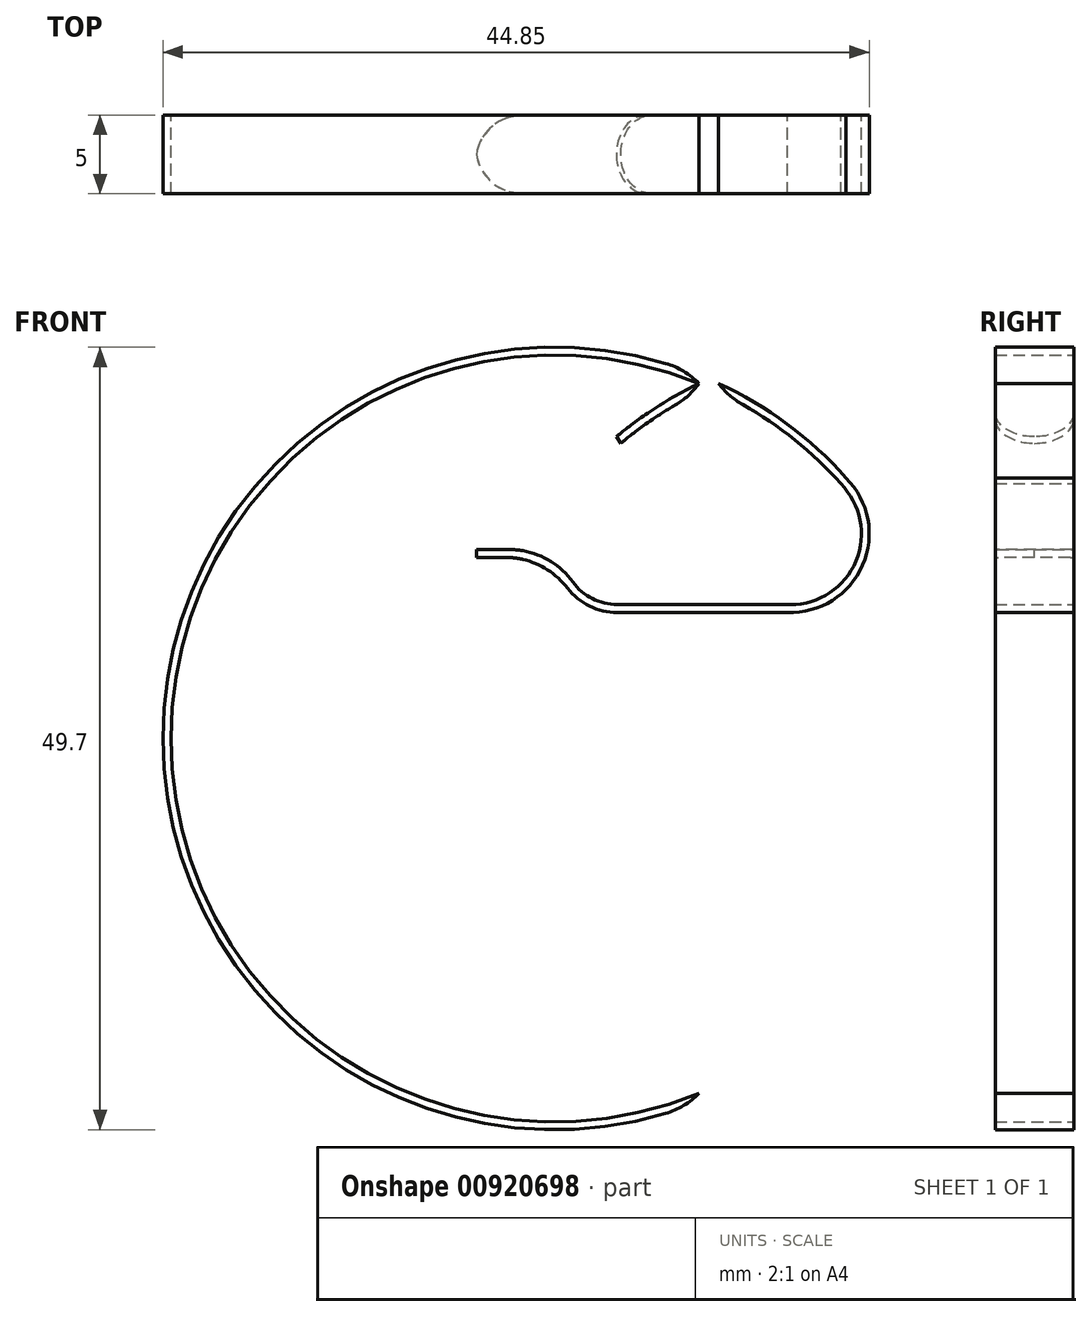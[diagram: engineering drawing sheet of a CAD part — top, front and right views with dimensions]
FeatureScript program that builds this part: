
annotation { "Feature Type Name" : "Feature", "Feature Type Description" : "" }
export const myFeature = defineFeature(function(context is Context, id is Id, definition is map)
    precondition{}
    {
        {
            var Q0;
            Q0=qCreatedBy(makeId("Front.planeOp"),FACE);
            var sketch = newSketch(context, id + "F0", { "sketchPlane" : qUnion([Q0])});
            skLineSegment(sketch, "E0.bottom", {"start": v(10, 7) * mm, "end": v(-10, 7) * mm});
            skLineSegment(sketch, "E0.top", {"start": v(10, -7) * mm, "end": v(-10, -7) * mm});
            skLineSegment(sketch, "E0.left", {"start": v(10, 7) * mm, "end": v(10, -7) * mm});
            skLineSegment(sketch, "E0.right", {"start": v(-10, 7) * mm, "end": v(-10, -7) * mm});
            skPoint(sketch, "E0.middle", {"position": v(0, 0) * mm});
            skLineSegment(sketch, "E1", {"start": v(10, -7) * mm, "end": v(5, -7) * mm});
            skLineSegment(sketch, "E2", {"start": v(5, -7) * mm, "end": v(5, -2) * mm});
            skCircle(sketch, "E3", {"center": v(5, -2) * mm, "radius": 5 * mm});
            skLineSegment(sketch, "E4", {"start": v(-10, -7) * mm, "end": v(-6, -7) * mm});
            skLineSegment(sketch, "E5", {"start": v(-6, -7) * mm, "end": v(-6, -3) * mm});
            skCircle(sketch, "E6", {"center": v(-6, -3) * mm, "radius": 4 * mm});
            skLineSegment(sketch, "E7", {"start": v(-10, -7) * mm, "end": v(-10, -15) * mm});
            skLineSegment(sketch, "E8", {"start": v(10, -7) * mm, "end": v(10, -15) * mm});
            skCircle(sketch, "E9", {"center": v(-10, -15) * mm, "radius": 24.85 * mm});
            skCircle(sketch, "E10", {"center": v(10, -15) * mm, "radius": 25 * mm});
            skCircle(sketch, "E11", {"center": v(-10, -15) * mm, "radius": 24.35 * mm});
            skCircle(sketch, "E12", {"center": v(10, -15) * mm, "radius": 24.5 * mm});
            skLineSegment(sketch, "E13", {"start": v(-6.06, 4.16) * mm, "end": v(-5.78, 3.74) * mm});
            skCircle(sketch, "E14", {"center": v(-6, -3) * mm, "radius": 3.5 * mm});
            skCircle(sketch, "E15", {"center": v(5, -2) * mm, "radius": 4.5 * mm});
            skLineSegment(sketch, "E16", {"start": v(-6, -3) * mm, "end": v(-15, -3) * mm});
            skLineSegment(sketch, "E17", {"start": v(-15, -3) * mm, "end": v(-15, -3.5) * mm});
            skLineSegment(sketch, "E18", {"start": v(-15, -3.5) * mm, "end": v(-6, -3.5) * mm});
            skLineSegment(sketch, "E19", {"start": v(-6, -6.5) * mm, "end": v(5, -6.5) * mm});
            skLineSegment(sketch, "E20", {"start": v(4.8, -6.37) * mm, "end": v(4.8, -7.22) * mm});
            skLineSegment(sketch, "E21", {"start": v(7.96, 0.92) * mm, "end": v(8.96, 2.01) * mm});
            skSolve(sketch);
        }
        {
            var Q0;
            {var subQ0=sQuery(id+"F0.wireOp",EDGE,"E3");var subQ3=makeQuery(id+"F0.imprint","INTERSECT",VERTEX,{"derivedFrom":[sQuery(id+"F0.wireOp",EDGE,"E0.left"),subQ0]});Q0=makeQuery(id+"F0.imprint","IMPRINT",FACE,{"disambiguationData":[TD([[makeQuery(id+"F0.imprint","IMPRINT",EDGE,{"disambiguationData":[TD([[subQ3,-1.0]])],"derivedFrom":subQ0}),1.0]])]});}
            var Q1;
            {var subQ0=sQuery(id+"F0.wireOp",EDGE,"E3");var subQ5=sQuery(id+"F0.wireOp",EDGE,"E20");var subQ6=makeQuery(id+"F0.imprint","INTERSECT",VERTEX,{"derivedFrom":[subQ0,subQ5]});Q1=makeQuery(id+"F0.imprint","IMPRINT",FACE,{"disambiguationData":[TD([[makeQuery(id+"F0.imprint","IMPRINT",EDGE,{"disambiguationData":[TD([[subQ6,1.0]])],"derivedFrom":subQ5}),1.0]])]});}
            var Q2;
            {var subQ0=sQuery(id+"F0.wireOp",EDGE,"E19");var subQ1=sQuery(id+"F0.wireOp",EDGE,"E3");var subQ2=makeQuery(id+"F0.imprint","INTERSECT",VERTEX,{"derivedFrom":[subQ1,subQ0]});Q2=makeQuery(id+"F0.imprint","IMPRINT",FACE,{"disambiguationData":[TD([[makeQuery(id+"F0.imprint","IMPRINT",EDGE,{"disambiguationData":[TD([[subQ2,-1.0]])],"derivedFrom":subQ1}),1.0]])]});}
            var Q3;
            {var subQ0=sQuery(id+"F0.wireOp",EDGE,"E19");var subQ1=sQuery(id+"F0.wireOp",EDGE,"E3");var subQ2=makeQuery(id+"F0.imprint","INTERSECT",VERTEX,{"derivedFrom":[subQ1,subQ0]});Q3=makeQuery(id+"F0.imprint","IMPRINT",FACE,{"disambiguationData":[TD([[makeQuery(id+"F0.imprint","IMPRINT",EDGE,{"disambiguationData":[TD([[subQ2,-1.0]])],"derivedFrom":subQ1}),-1.0]])]});}
            var Q4;
            {var subQ0=sQuery(id+"F0.wireOp",EDGE,"E11");var subQ1=sQuery(id+"F0.wireOp",EDGE,"E3");var subQ2=makeQuery(id+"F0.imprint","INTERSECT",VERTEX,{"disambiguationData":[OD(0.0)],"derivedFrom":[subQ1,subQ0]});Q4=makeQuery(id+"F0.imprint","IMPRINT",FACE,{"disambiguationData":[TD([[makeQuery(id+"F0.imprint","IMPRINT",EDGE,{"disambiguationData":[TD([[subQ2,-1.0]])],"derivedFrom":subQ1}),1.0]])]});}
            var Q5;
            {var subQ0=sQuery(id+"F0.wireOp",EDGE,"E21");var subQ1=sQuery(id+"F0.wireOp",EDGE,"E3");var subQ2=makeQuery(id+"F0.imprint","INTERSECT",VERTEX,{"derivedFrom":[subQ1,subQ0]});Q5=makeQuery(id+"F0.imprint","IMPRINT",FACE,{"disambiguationData":[TD([[makeQuery(id+"F0.imprint","IMPRINT",EDGE,{"disambiguationData":[TD([[subQ2,-1.0]])],"derivedFrom":subQ1}),1.0]])]});}
            var Q6;
            {var subQ1=sQuery(id+"F0.wireOp",EDGE,"E0.bottom");var subQ7=sQuery(id+"F0.wireOp",EDGE,"E9");var subQ9=makeQuery(id+"F0.imprint","INTERSECT",VERTEX,{"derivedFrom":[subQ1,subQ7]});Q6=makeQuery(id+"F0.imprint","IMPRINT",FACE,{"disambiguationData":[TD([[makeQuery(id+"F0.imprint","IMPRINT",EDGE,{"disambiguationData":[TD([[subQ9,-1.0]])],"derivedFrom":subQ1}),1.0]])]});}
            var Q7;
            {var subQ0=sQuery(id+"F0.wireOp",EDGE,"E6");var subQ3=sQuery(id+"F0.wireOp",EDGE,"E19");var subQ5=makeQuery(id+"F0.imprint","INTERSECT",VERTEX,{"derivedFrom":[subQ0,subQ3]});Q7=makeQuery(id+"F0.imprint","IMPRINT",FACE,{"disambiguationData":[TD([[makeQuery(id+"F0.imprint","IMPRINT",EDGE,{"disambiguationData":[TD([[subQ5,1.0]])],"derivedFrom":subQ3}),-1.0]])]});}
            var Q8;
            {var subQ0=sQuery(id+"F0.wireOp",EDGE,"E6");var subQ5=sQuery(id+"F0.wireOp",EDGE,"E18");var subQ6=makeQuery(id+"F0.imprint","INTERSECT",VERTEX,{"derivedFrom":[subQ0,subQ5]});Q8=makeQuery(id+"F0.imprint","IMPRINT",FACE,{"disambiguationData":[TD([[makeQuery(id+"F0.imprint","IMPRINT",EDGE,{"disambiguationData":[TD([[subQ6,-1.0]])],"derivedFrom":subQ5}),-1.0]])]});}
            var Q9;
            {var subQ0=sQuery(id+"F0.wireOp",EDGE,"E18");var subQ5=sQuery(id+"F0.wireOp",EDGE,"E14");var subQ6=makeQuery(id+"F0.imprint","INTERSECT",VERTEX,{"derivedFrom":[subQ5,subQ0]});Q9=makeQuery(id+"F0.imprint","IMPRINT",FACE,{"disambiguationData":[TD([[makeQuery(id+"F0.imprint","IMPRINT",EDGE,{"disambiguationData":[TD([[subQ6,1.0]])],"derivedFrom":subQ5}),-1.0]])]});}
            var Q10;
            {var subQ0=sQuery(id+"F0.wireOp",EDGE,"E18");var subQ1=sQuery(id+"F0.wireOp",EDGE,"E0.right");var subQ2=makeQuery(id+"F0.imprint","INTERSECT",VERTEX,{"derivedFrom":[subQ1,subQ0]});Q10=makeQuery(id+"F0.imprint","IMPRINT",FACE,{"disambiguationData":[TD([[makeQuery(id+"F0.imprint","IMPRINT",EDGE,{"disambiguationData":[TD([[subQ2,-1.0]])],"derivedFrom":subQ0}),1.0]])]});}
            var Q11;
            {var subQ3=sQuery(id+"F0.wireOp",EDGE,"E16");var subQ5=sQuery(id+"F0.wireOp",EDGE,"E12");var subQ7=makeQuery(id+"F0.imprint","INTERSECT",VERTEX,{"derivedFrom":[subQ5,subQ3]});Q11=makeQuery(id+"F0.imprint","IMPRINT",FACE,{"disambiguationData":[TD([[makeQuery(id+"F0.imprint","IMPRINT",EDGE,{"disambiguationData":[TD([[subQ7,-1.0]])],"derivedFrom":subQ5}),1.0]])]});}
            var Q12;
            {var subQ0=sQuery(id+"F0.wireOp",EDGE,"E16");var subQ1=sQuery(id+"F0.wireOp",EDGE,"E10");var subQ2=makeQuery(id+"F0.imprint","INTERSECT",VERTEX,{"derivedFrom":[subQ1,subQ0]});Q12=makeQuery(id+"F0.imprint","IMPRINT",FACE,{"disambiguationData":[TD([[makeQuery(id+"F0.imprint","IMPRINT",EDGE,{"disambiguationData":[TD([[subQ2,-1.0]])],"derivedFrom":subQ1}),1.0]])]});}
            var Q13;
            {var subQ5=sQuery(id+"F0.wireOp",EDGE,"E17");Q13=makeQuery(id+"F0.imprint","IMPRINT",FACE,{"disambiguationData":[TD([[makeQuery(id+"F0.imprint","IMPRINT",EDGE,{"derivedFrom":subQ5}),1.0]])]});}
            var Q14;
            {var subQ0=sQuery(id+"F0.wireOp",EDGE,"E9");var subQ1=sQuery(id+"F0.wireOp",EDGE,"E0.bottom");var subQ2=makeQuery(id+"F0.imprint","INTERSECT",VERTEX,{"derivedFrom":[subQ1,subQ0]});Q14=makeQuery(id+"F0.imprint","IMPRINT",FACE,{"disambiguationData":[TD([[makeQuery(id+"F0.imprint","IMPRINT",EDGE,{"disambiguationData":[TD([[subQ2,-1.0]])],"derivedFrom":subQ1}),-1.0]])]});}
            var Q15;
            {var subQ0=sQuery(id+"F0.wireOp",EDGE,"E10");var subQ1=sQuery(id+"F0.wireOp",EDGE,"E9");var subQ2=makeQuery(id+"F0.imprint","INTERSECT",VERTEX,{"disambiguationData":[OD(0.0)],"derivedFrom":[subQ1,subQ0]});Q15=makeQuery(id+"F0.imprint","IMPRINT",FACE,{"disambiguationData":[TD([[makeQuery(id+"F0.imprint","IMPRINT",EDGE,{"disambiguationData":[TD([[subQ2,1.0]])],"derivedFrom":subQ1}),1.0]])]});}
            var Q16;
            {var subQ0=sQuery(id+"F0.wireOp",EDGE,"E12");var subQ1=sQuery(id+"F0.wireOp",EDGE,"E0.bottom");var subQ2=makeQuery(id+"F0.imprint","INTERSECT",VERTEX,{"derivedFrom":[subQ1,subQ0]});Q16=makeQuery(id+"F0.imprint","IMPRINT",FACE,{"disambiguationData":[TD([[makeQuery(id+"F0.imprint","IMPRINT",EDGE,{"disambiguationData":[TD([[subQ2,-1.0]])],"derivedFrom":subQ1}),-1.0]])]});}
            var Q17;
            {var subQ5=sQuery(id+"F0.wireOp",EDGE,"E13");Q17=makeQuery(id+"F0.imprint","IMPRINT",FACE,{"disambiguationData":[TD([[makeQuery(id+"F0.imprint","IMPRINT",EDGE,{"derivedFrom":subQ5}),1.0]])]});}
            extrude(context, id + "F1", {"entities" : qUnion([Q0, Q1, Q2, Q3, Q4, Q5, Q6, Q7, Q8, Q9, Q10, Q11, Q12, Q13, Q14, Q15, Q16, Q17]), "depth" : 5 * mm, "offsetDistance" : 25 * mm});
        }
        {
            var Q0;
            Q0=makeQuery(id+"F1.opExtrude","SWEPT_EDGE",EDGE,{"disambiguationData":[OSD([sQuery(id+"F0.wireOp",EDGE,"E6"),sQuery(id+"F0.wireOp",EDGE,"E18")])]});
            fillet(context, id + "F2", {"entities" : qUnion([Q0]), "radius" : 5 * mm, "tangentPropagation" : true, "allowEdgeOverflow" : false});
        }
        {
            var Q0;
            Q0=makeQuery(id+"F1.opExtrude","SWEPT_EDGE",EDGE,{"disambiguationData":[OSD([sQuery(id+"F0.wireOp",EDGE,"E14"),sQuery(id+"F0.wireOp",EDGE,"E16")])]});
            fillet(context, id + "F3", {"entities" : qUnion([Q0]), "radius" : 5 * mm, "tangentPropagation" : true, "allowEdgeOverflow" : false});
        }
        {
            var Q0;
            Q0=makeQuery(id+"F1.opExtrude","SWEPT_EDGE",EDGE,{"disambiguationData":[OSD([sQuery(id+"F0.wireOp",EDGE,"E11"),sQuery(id+"F0.wireOp",EDGE,"E12")])]});
            fillet(context, id + "F4", {"entities" : qUnion([Q0]), "radius" : 5 * mm, "tangentPropagation" : true, "allowEdgeOverflow" : false});
        }
        {
            var Q0;
            Q0=makeQuery(id+"F1.opExtrude","SWEPT_EDGE",EDGE,{"disambiguationData":[OSD([sQuery(id+"F0.wireOp",EDGE,"E9"),sQuery(id+"F0.wireOp",EDGE,"E10")])]});
            fillet(context, id + "F5", {"entities" : qUnion([Q0]), "radius" : 5 * mm, "tangentPropagation" : true, "allowEdgeOverflow" : false});
        }
        {
            var Q0;
            Q0=makeQuery(id+"F1.opExtrude","CAP_EDGE",EDGE,{"disambiguationData":[OSD([sQuery(id+"F0.wireOp",EDGE,"E13")])],"isStart":false});
            var Q1;
            Q1=makeQuery(id+"F1.opExtrude","CAP_EDGE",EDGE,{"disambiguationData":[OSD([sQuery(id+"F0.wireOp",EDGE,"E13")])],"isStart":true});
            fillet(context, id + "F6", {"entities" : qUnion([Q0, Q1]), "radius" : 2.5 * mm, "tangentPropagation" : true, "allowEdgeOverflow" : false});
        }
        {
            var Q0;
            Q0=makeQuery(id+"F1.opExtrude","CAP_EDGE",EDGE,{"disambiguationData":[OSD([sQuery(id+"F0.wireOp",EDGE,"E17")])],"isStart":false});
            var Q1;
            Q1=makeQuery(id+"F1.opExtrude","CAP_EDGE",EDGE,{"disambiguationData":[OSD([sQuery(id+"F0.wireOp",EDGE,"E17")])],"isStart":true});
            fillet(context, id + "F7", {"entities" : qUnion([Q0, Q1]), "radius" : 3 * mm, "tangentPropagation" : true, "allowEdgeOverflow" : false});
        }
    });
